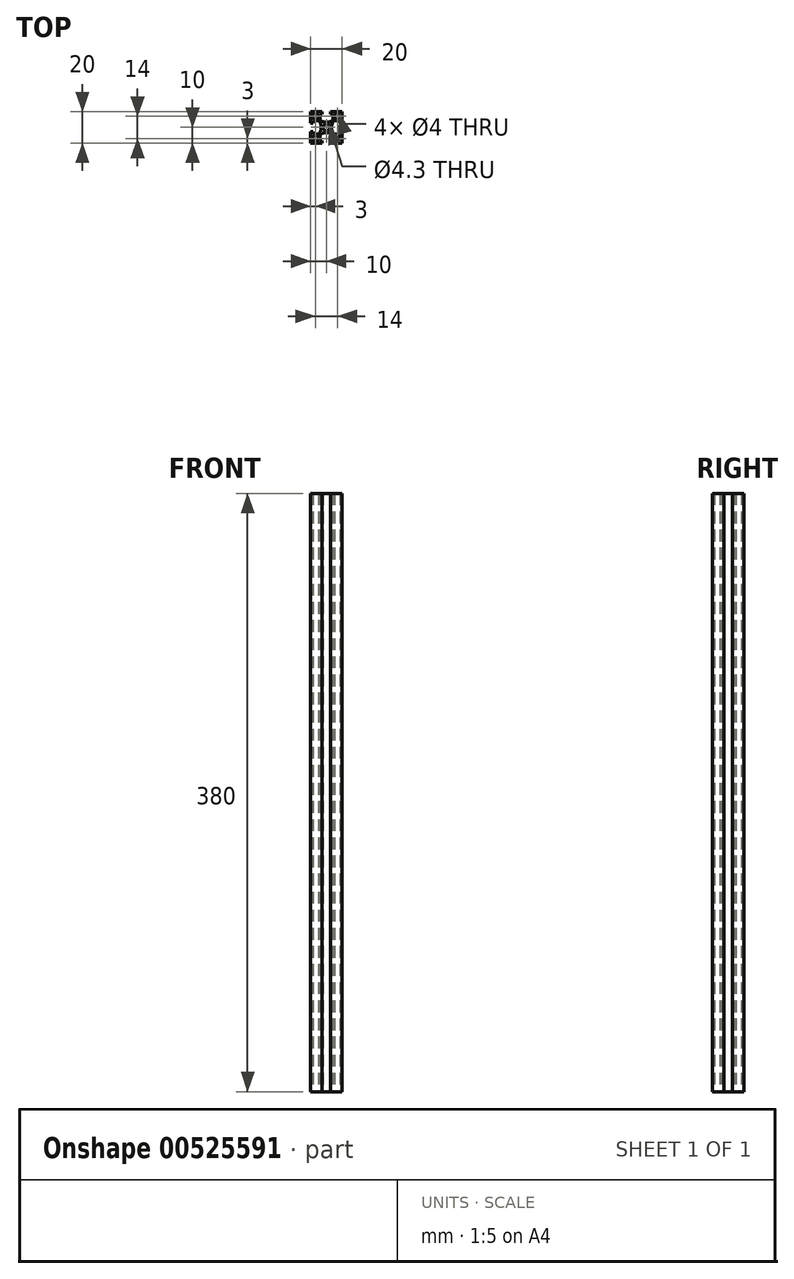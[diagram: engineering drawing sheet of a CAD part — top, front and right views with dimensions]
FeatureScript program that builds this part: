
annotation { "Feature Type Name" : "Feature", "Feature Type Description" : "" }
export const myFeature = defineFeature(function(context is Context, id is Id, definition is map)
    precondition{}
    {
        {
            var Q0;
            Q0=qCreatedBy(makeId("Top.planeOp"),FACE);
            var sketch = newSketch(context, id + "F0", { "sketchPlane" : qUnion([Q0])});
            skCircle(sketch, "E0", {"center": v(-7, 7) * mm, "radius": 2 * mm});
            skCircle(sketch, "E1.MirrorC", {"center": v(-7, -7) * mm, "radius": 2 * mm});
            skLineSegment(sketch, "E2.top", {"start": v(-10, 2.65) * mm, "end": v(-10, -2.65) * mm});
            skLineSegment(sketch, "E2.left", {"start": v(-8.5, 2.65) * mm, "end": v(-10, 2.65) * mm});
            skLineSegment(sketch, "E2.right", {"start": v(-8.5, -2.65) * mm, "end": v(-10, -2.65) * mm});
            skLineSegment(sketch, "E3.bottom", {"start": v(-8.5, 4.15) * mm, "end": v(-8.5, 2.65) * mm});
            skLineSegment(sketch, "E3.left", {"start": v(-8.5, 4.15) * mm, "end": v(-4.55, 4.15) * mm});
            skLineSegment(sketch, "E3.right", {"start": v(-8.5, -4.15) * mm, "end": v(-4.55, -4.15) * mm});
            skArc(sketch, "E4", {"start": v(-4.55, -4.15) * mm, "mid": v(-3.3, 0) * mm, "end": v(-4.55, 4.15) * mm});
            skLineSegment(sketch, "E5.trimOffspring", {"start": v(-8.5, -2.65) * mm, "end": v(-8.5, -4.15) * mm});
            skLineSegment(sketch, "E6.bottom", {"start": v(10, -10) * mm, "end": v(-10, -10) * mm});
            skLineSegment(sketch, "E6.top", {"start": v(10, 10) * mm, "end": v(-10, 10) * mm});
            skLineSegment(sketch, "E6.left", {"start": v(10, -10) * mm, "end": v(10, 10) * mm});
            skLineSegment(sketch, "E6.right", {"start": v(-10, -10) * mm, "end": v(-10, 10) * mm});
            skPoint(sketch, "E6.middle", {"position": v(0, 0) * mm});
            skCircle(sketch, "E7.MirrorC", {"center": v(7, 7) * mm, "radius": 2 * mm});
            skCircle(sketch, "E8.MirrorC", {"center": v(7, -7) * mm, "radius": 2 * mm});
            skLineSegment(sketch, "E9.1.0", {"start": v(-4.15, -8.5) * mm, "end": v(-2.65, -8.5) * mm});
            skArc(sketch, "E9.1.1", {"start": v(4.15, -4.55) * mm, "mid": v(0, -3.3) * mm, "end": v(-4.15, -4.55) * mm});
            skLineSegment(sketch, "E9.1.2", {"start": v(-2.65, -10) * mm, "end": v(2.65, -10) * mm});
            skLineSegment(sketch, "E9.1.3", {"start": v(-2.65, -8.5) * mm, "end": v(-2.65, -10) * mm});
            skLineSegment(sketch, "E9.1.4", {"start": v(-4.15, -8.5) * mm, "end": v(-4.15, -4.55) * mm});
            skLineSegment(sketch, "E9.1.5", {"start": v(2.65, -8.5) * mm, "end": v(4.15, -8.5) * mm});
            skLineSegment(sketch, "E9.1.6", {"start": v(4.15, -8.5) * mm, "end": v(4.15, -4.55) * mm});
            skLineSegment(sketch, "E9.1.7", {"start": v(2.65, -8.5) * mm, "end": v(2.65, -10) * mm});
            skLineSegment(sketch, "E9.2.0", {"start": v(8.5, -4.15) * mm, "end": v(8.5, -2.65) * mm});
            skArc(sketch, "E9.2.1", {"start": v(4.55, 4.15) * mm, "mid": v(3.3, 0) * mm, "end": v(4.55, -4.15) * mm});
            skLineSegment(sketch, "E9.2.2", {"start": v(10, -2.65) * mm, "end": v(10, 2.65) * mm});
            skLineSegment(sketch, "E9.2.3", {"start": v(8.5, -2.65) * mm, "end": v(10, -2.65) * mm});
            skLineSegment(sketch, "E9.2.4", {"start": v(8.5, -4.15) * mm, "end": v(4.55, -4.15) * mm});
            skLineSegment(sketch, "E9.2.5", {"start": v(8.5, 2.65) * mm, "end": v(8.5, 4.15) * mm});
            skLineSegment(sketch, "E9.2.6", {"start": v(8.5, 4.15) * mm, "end": v(4.55, 4.15) * mm});
            skLineSegment(sketch, "E9.2.7", {"start": v(8.5, 2.65) * mm, "end": v(10, 2.65) * mm});
            skLineSegment(sketch, "E9.3.0", {"start": v(4.15, 8.5) * mm, "end": v(2.65, 8.5) * mm});
            skArc(sketch, "E9.3.1", {"start": v(-4.15, 4.55) * mm, "mid": v(0, 3.3) * mm, "end": v(4.15, 4.55) * mm});
            skLineSegment(sketch, "E9.3.2", {"start": v(2.65, 10) * mm, "end": v(-2.65, 10) * mm});
            skLineSegment(sketch, "E9.3.3", {"start": v(2.65, 8.5) * mm, "end": v(2.65, 10) * mm});
            skLineSegment(sketch, "E9.3.4", {"start": v(4.15, 8.5) * mm, "end": v(4.15, 4.55) * mm});
            skLineSegment(sketch, "E9.3.5", {"start": v(-2.65, 8.5) * mm, "end": v(-4.15, 8.5) * mm});
            skLineSegment(sketch, "E9.3.6", {"start": v(-4.15, 8.5) * mm, "end": v(-4.15, 4.55) * mm});
            skLineSegment(sketch, "E9.3.7", {"start": v(-2.65, 8.5) * mm, "end": v(-2.65, 10) * mm});
            skCircle(sketch, "E10", {"center": v(0, 0) * mm, "radius": 2.15 * mm});
            skSolve(sketch);
        }
        {
            var Q0;
            Q0=makeQuery(id+"F0.imprint","IMPRINT",FACE,{"disambiguationData":[TD([[makeQuery(id+"F0.imprint","IMPRINT",EDGE,{"derivedFrom":sQuery(id+"F0.wireOp",EDGE,"E0")}),-1.0]])]});
            extrude(context, id + "F1", {"entities" : qUnion([Q0]), "depth" : 380 * mm, "offsetDistance" : 25 * mm});
        }
    });
